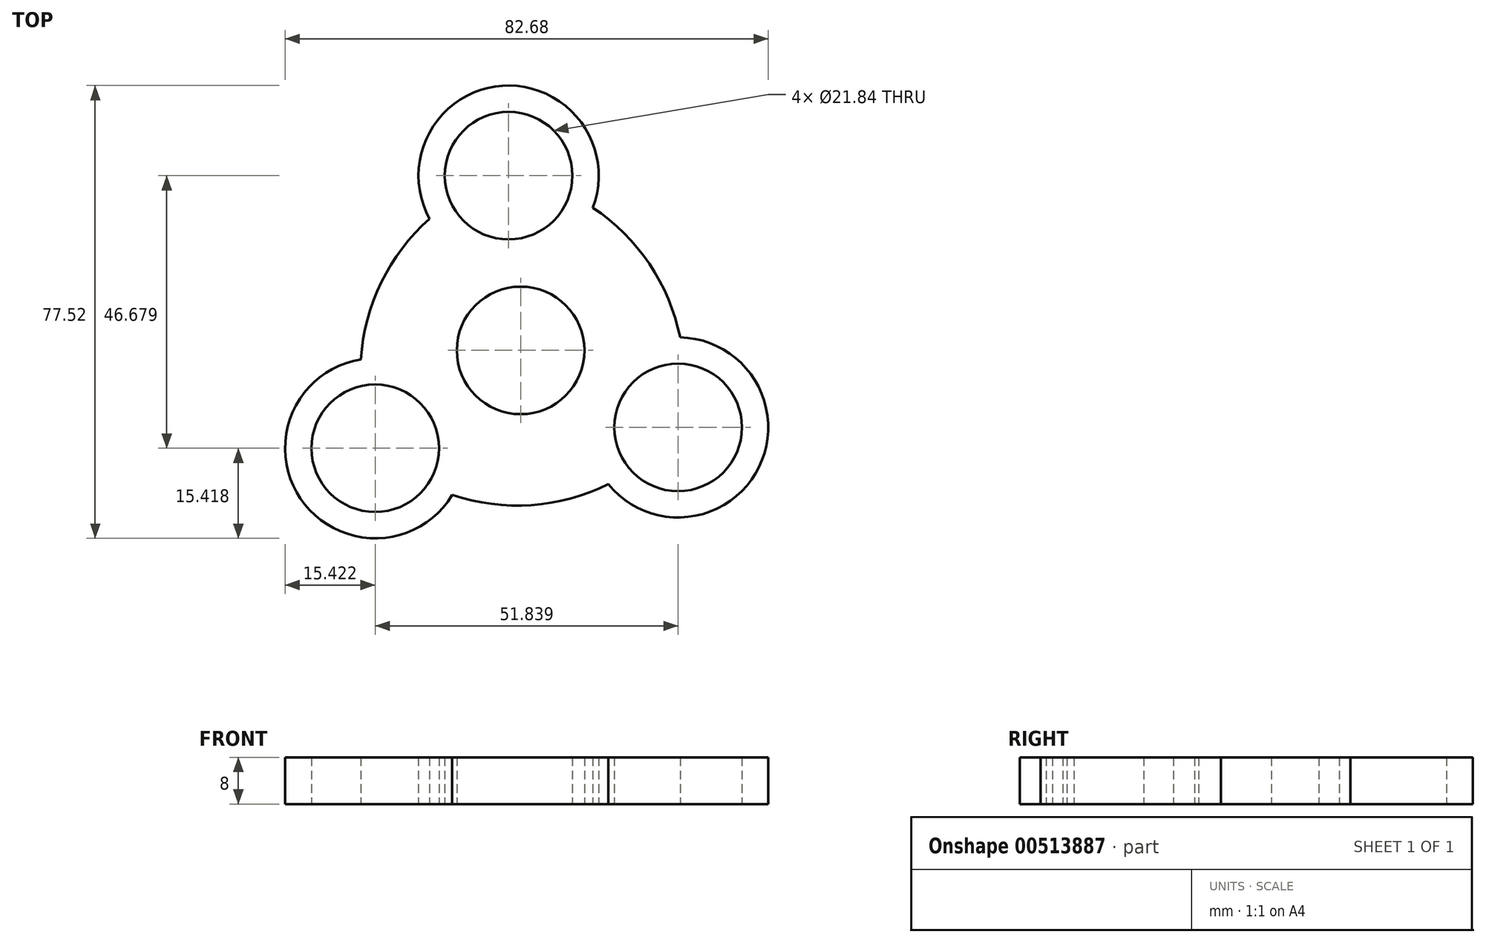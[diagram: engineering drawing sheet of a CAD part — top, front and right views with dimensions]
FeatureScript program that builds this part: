
annotation { "Feature Type Name" : "Feature", "Feature Type Description" : "" }
export const myFeature = defineFeature(function(context is Context, id is Id, definition is map)
    precondition{}
    {
        {
            var Q0;
            Q0=qCreatedBy(makeId("Top.planeOp"),FACE);
            var sketch = newSketch(context, id + "F0", { "sketchPlane" : qUnion([Q0])});
            skCircle(sketch, "E0", {"center": v(0, 50.66) * mm, "radius": 10.92 * mm});
            skCircle(sketch, "E1.1.0", {"center": v(29.01, 7.55) * mm, "radius": 10.92 * mm});
            skCircle(sketch, "E1.2.0", {"center": v(-22.83, 3.98) * mm, "radius": 10.92 * mm});
            skCircle(sketch, "E2", {"center": v(2.06, 20.73) * mm, "radius": 10.92 * mm});
            skArc(sketch, "E3.trimOffspring", {"start": v(-10.83, 49.27) * mm, "mid": v(-10.86, 49.63) * mm, "end": v(-10.9, 50) * mm});
            skArc(sketch, "E4", {"start": v(17.05, -2.19) * mm, "mid": v(42.86, 0.77) * mm, "end": v(29.35, 22.96) * mm});
            skArc(sketch, "E5", {"start": v(-25.28, 19.2) * mm, "mid": v(-35.62, -4.63) * mm, "end": v(-9.65, -4.02) * mm});
            skArc(sketch, "E6", {"start": v(14.4, 45.17) * mm, "mid": v(-1.06, 66.04) * mm, "end": v(-13.52, 43.24) * mm});
            skArc(sketch, "E7", {"start": v(29.97, 18.43) * mm, "mid": v(25.3, 33.6) * mm, "end": v(14.4, 45.17) * mm});
            skArc(sketch, "E8", {"start": v(-9.65, -4.02) * mm, "mid": v(6.16, -5.53) * mm, "end": v(21.01, 0.12) * mm});
            skArc(sketch, "E9.trimOffspring", {"start": v(-13.52, 43.24) * mm, "mid": v(-21.79, 32.4) * mm, "end": v(-25.28, 19.2) * mm});
            skSolve(sketch);
        }
        {
            var Q0;
            Q0 = qSketchRegion(id + "F0", true);
            extrude(context, id + "F1", {"entities" : qUnion([Q0]), "depth" : 8 * mm, "offsetDistance" : 25 * mm});
        }
    });
